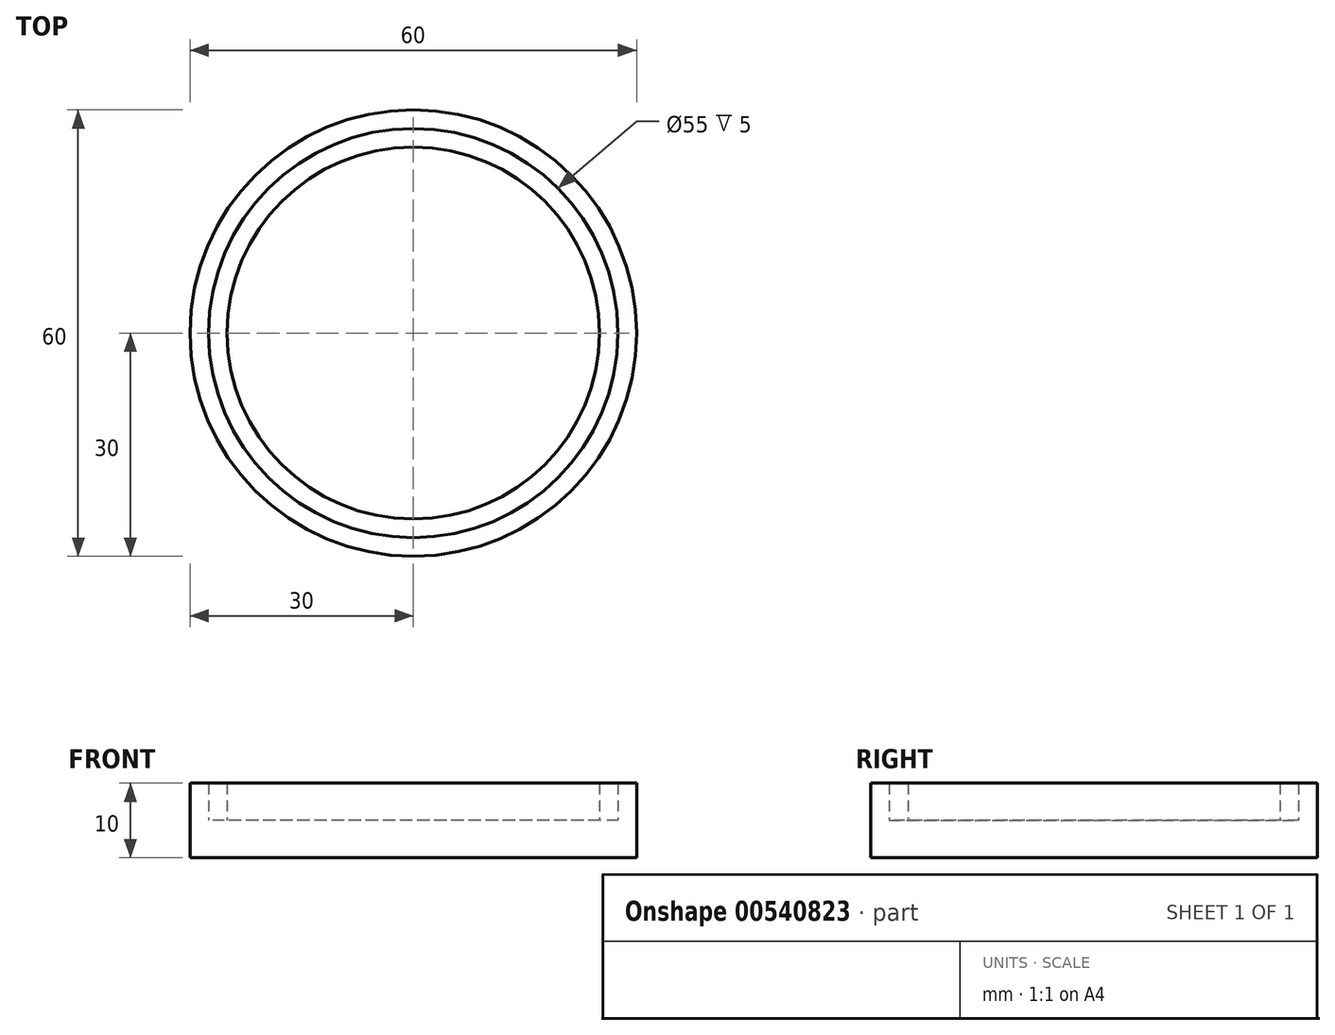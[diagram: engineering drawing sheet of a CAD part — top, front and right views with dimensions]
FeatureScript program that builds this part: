
annotation { "Feature Type Name" : "Feature", "Feature Type Description" : "" }
export const myFeature = defineFeature(function(context is Context, id is Id, definition is map)
    precondition{}
    {
        {
            var Q0;
            Q0=qCreatedBy(makeId("Top.planeOp"),FACE);
            var sketch = newSketch(context, id + "F0", { "sketchPlane" : qUnion([Q0])});
            skCircle(sketch, "E0", {"center": v(0, 0) * mm, "radius": 30 * mm});
            skCircle(sketch, "E1", {"center": v(0, 0) * mm, "radius": 27.5 * mm});
            skSolve(sketch);
        }
        {
            var Q0;
            Q0=makeQuery(id+"F0.imprint","IMPRINT",FACE,{"disambiguationData":[TD([[makeQuery(id+"F0.imprint","IMPRINT",EDGE,{"derivedFrom":sQuery(id+"F0.wireOp",EDGE,"E0")}),1.0]])]});
            var Q1;
            Q1=makeQuery(id+"F0.imprint","IMPRINT",FACE,{"disambiguationData":[TD([[makeQuery(id+"F0.imprint","IMPRINT",EDGE,{"derivedFrom":sQuery(id+"F0.wireOp",EDGE,"TKAMxMoK-uBKS-kygp-Y8Bh-TORWD2d1Qmyf")}),1.0]])]});
            extrude(context, id + "F1", {"entities" : qUnion([Q0, Q1]), "depth" : 5 * mm, "offsetDistance" : 25 * mm});
        }
        {
            var Q0;
            Q0 = qSketchRegion(id + "F0", true);
            extrude(context, id + "F2", {"entities" : qUnion([Q0]), "operationType" : NewBodyOperationType.ADD, "depth" : 10 * mm, "offsetDistance" : 25 * mm});
        }
        {
            var Q0;
            Q0 = qSketchRegion(id + "F0", true);
            extrude(context, id + "F3", {"entities" : qUnion([Q0]), "operationType" : NewBodyOperationType.ADD, "depth" : 7.5 * mm, "offsetDistance" : 25 * mm});
        }
        {
            var Q0;
            Q0=qCreatedBy(makeId("Top.planeOp"),FACE);
            var sketch = newSketch(context, id + "F4", { "sketchPlane" : qUnion([Q0])});
            skCircle(sketch, "E2", {"center": v(0, 0) * mm, "radius": 30 * mm});
            skSolve(sketch);
        }
        {
            var Q0;
            Q0 = qSketchRegion(id + "F4", true);
            extrude(context, id + "F5", {"entities" : qUnion([Q0]), "operationType" : NewBodyOperationType.ADD, "depth" : 5 * mm, "offsetDistance" : 25 * mm});
        }
        {
            var Q0;
            Q0=qCreatedBy(makeId("Top.planeOp"),FACE);
            var sketch = newSketch(context, id + "F6", { "sketchPlane" : qUnion([Q0])});
            skCircle(sketch, "E3", {"center": v(0, 0) * mm, "radius": 30 * mm});
            skCircle(sketch, "E4", {"center": v(0, 0) * mm, "radius": 27.5 * mm});
            skSolve(sketch);
        }
        {
            var Q0;
            Q0 = qSketchRegion(id + "F6", true);
            extrude(context, id + "F7", {"entities" : qUnion([Q0]), "operationType" : NewBodyOperationType.ADD, "depth" : 2.5 * mm, "offsetDistance" : 25 * mm});
        }
        {
            var Q0;
            Q0=qCreatedBy(makeId("Top.planeOp"),FACE);
            var sketch = newSketch(context, id + "F8", { "sketchPlane" : qUnion([Q0])});
            skCircle(sketch, "E5", {"center": v(0, 0) * mm, "radius": 17.5 * mm});
            skSolve(sketch);
        }
        {
            var Q0;
            Q0 = qSketchRegion(id + "F8", true);
            extrude(context, id + "F9", {"entities" : qUnion([Q0]), "operationType" : NewBodyOperationType.ADD, "depth" : 3 * mm, "offsetDistance" : 25 * mm});
        }
        {
            var Q0;
            Q0=qCreatedBy(makeId("Top.planeOp"),FACE);
            var sketch = newSketch(context, id + "F10", { "sketchPlane" : qUnion([Q0])});
            skCircle(sketch, "E6", {"center": v(0, 0) * mm, "radius": 25 * mm});
            skSolve(sketch);
        }
        {
            var Q0;
            Q0 = qSketchRegion(id + "F10", true);
            extrude(context, id + "F11", {"entities" : qUnion([Q0]), "operationType" : NewBodyOperationType.ADD, "depth" : 10 * mm, "offsetDistance" : 25 * mm});
        }
    });
